# Revit family: ASSA_ABLOY_DockLeveler_DL6120T
name_source: partatom
category: Specialty Equipment
units: mm (PartAtom-declared; Revit-internal decimal feet)

## family parameters
Always vertical = Yes
Cut with Voids When Loaded = No
Host = Floor
Part Type = Normal
Room Calculation Point = No
Round Connector Dimension = Use Diameter
Shared = No

## types (3) — shared parameters
DL6120T_LipErgoSteelLL345 = DL6120T_LevelerTop : DL6120T_LipErgoSteelLL345
DL6120T_LipSteelLL1000 = DL6120T_LevelerTop : DL6120T_LipSteelLL1000
DL6120T_LipSteelLL500 = DL6120T_LevelerTop : DL6120T_LipSteelLL500
Description = Docking Leveler
Manufacturer = ASSA ABLOY
Model = DL6120T
TailLiftWidth = 3000 mm  [stored 9.84252 ft]

## per-type parameters (varying)
| type | LipType | URL |
| Lip Ergo Steel LL345 | DL6120T_LevelerTop : DL6120T_LipErgoSteelLL345 | https://www.assaabloyentrance.com |
| Lip Steel LL1000 | DL6120T_LevelerTop : DL6120T_LipSteelLL1000 |  |
| Lip Steel LL500 | DL6120T_LevelerTop : DL6120T_LipSteelLL500 |  |

note: [stored X ft] marks values corroborated as IEEE doubles in the binary element streams (Revit-internal decimal feet)

## geometry (parser evidence)
native form markers: Sweep x6
no freeform markers — native parametric forms only
